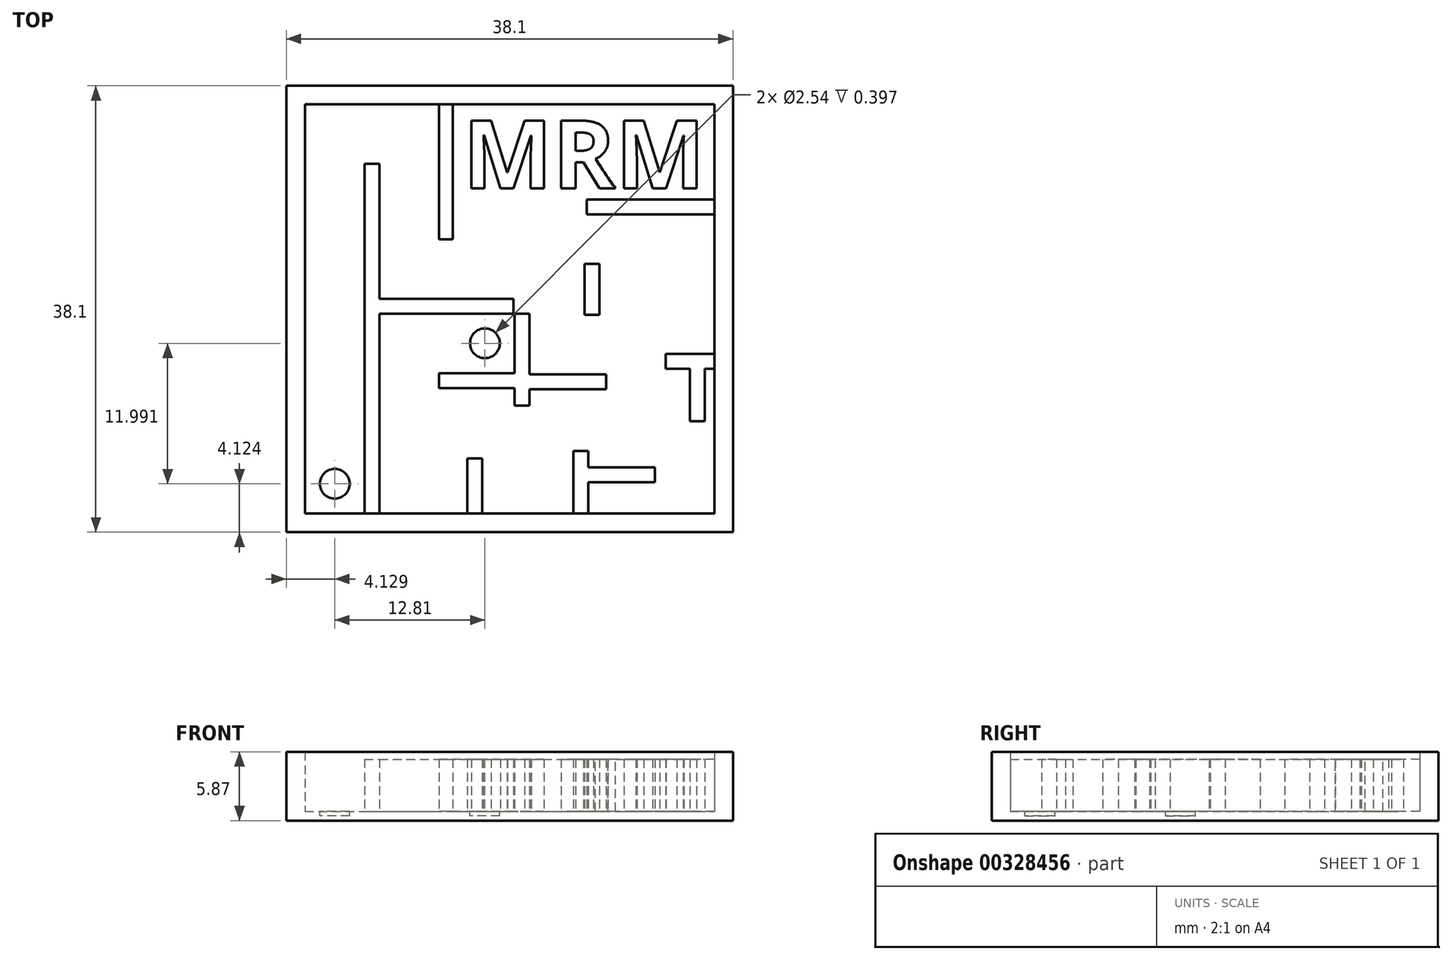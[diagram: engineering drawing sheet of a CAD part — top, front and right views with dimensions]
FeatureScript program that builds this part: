
annotation { "Feature Type Name" : "Feature", "Feature Type Description" : "" }
export const myFeature = defineFeature(function(context is Context, id is Id, definition is map)
    precondition{}
    {
        {
            var Q0;
            Q0=qCreatedBy(makeId("Top.planeOp"),FACE);
            var sketch = newSketch(context, id + "F0", { "sketchPlane" : qUnion([Q0])});
            skLineSegment(sketch, "E0.bottom", {"start": v(-20, 23.3) * mm, "end": v(18.1, 23.3) * mm});
            skLineSegment(sketch, "E0.top", {"start": v(-20, -14.8) * mm, "end": v(18.1, -14.8) * mm});
            skLineSegment(sketch, "E0.left", {"start": v(-20, 23.3) * mm, "end": v(-20, -14.8) * mm});
            skLineSegment(sketch, "E0.right", {"start": v(18.1, 23.3) * mm, "end": v(18.1, -14.8) * mm});
            skSolve(sketch);
        }
        {
            var Q0;
            Q0=makeQuery(id+"F0.imprint","IMPRINT",FACE,{"disambiguationData":[TD([[makeQuery(id+"F0.imprint","IMPRINT",EDGE,{"derivedFrom":sQuery(id+"F0.wireOp",EDGE,"E0.bottom")}),-1.0]])]});
            extrude(context, id + "F1", {"entities" : qUnion([Q0]), "oppositeDirection" : true, "depth" : 0.8 * mm});
        }
        {
            var Q0;
            Q0=makeQuery(id+"F1.opExtrude","CAP_FACE",FACE,{"disambiguationData":[OSD([sQuery(id+"F0.wireOp",EDGE,"E0.bottom"),sQuery(id+"F0.wireOp",EDGE,"E0.top"),sQuery(id+"F0.wireOp",EDGE,"E0.left"),sQuery(id+"F0.wireOp",EDGE,"E0.right")])],"isStart":true});
            var sketch = newSketch(context, id + "F2", { "sketchPlane" : qUnion([Q0])});
            skLineSegment(sketch, "E1.0", {"start": v(-18.42, 21.7) * mm, "end": v(16.5, 21.7) * mm});
            skLineSegment(sketch, "E1.1", {"start": v(-18.42, 21.7) * mm, "end": v(-18.42, -13.22) * mm});
            skLineSegment(sketch, "E1.2", {"start": v(-18.42, -13.22) * mm, "end": v(16.5, -13.22) * mm});
            skLineSegment(sketch, "E1.3", {"start": v(16.5, 21.7) * mm, "end": v(16.5, -13.22) * mm});
            skSolve(sketch);
        }
        {
            var Q0;
            Q0=makeQuery(id+"F2.imprint","IMPRINT",FACE,{"disambiguationData":[TD([[makeQuery(id+"F2.imprint","IMPRINT",EDGE,{"derivedFrom":sQuery(id+"F2.wireOp",EDGE,"E1.0")}),1.0]])]});
            extrude(context, id + "F3", {"entities" : qUnion([Q0]), "operationType" : NewBodyOperationType.ADD, "depth" : 5.08 * mm});
        }
        {
            var Q0;
            Q0=makeQuery(id+"F1.opExtrude","CAP_FACE",FACE,{"disambiguationData":[OSD([sQuery(id+"F0.wireOp",EDGE,"E0.bottom"),sQuery(id+"F0.wireOp",EDGE,"E0.top"),sQuery(id+"F0.wireOp",EDGE,"E0.left"),sQuery(id+"F0.wireOp",EDGE,"E0.right")])],"isStart":true});
            var sketch = newSketch(context, id + "F4", { "sketchPlane" : qUnion([Q0])});
            skLineSegment(sketch, "E2.bottom", {"start": v(-13.34, -13.22) * mm, "end": v(-12.07, -13.22) * mm});
            skLineSegment(sketch, "E2.top", {"start": v(-13.34, 16.63) * mm, "end": v(-12.07, 16.63) * mm});
            skLineSegment(sketch, "E2.left", {"start": v(-13.34, -13.22) * mm, "end": v(-13.34, 16.63) * mm});
            skLineSegment(sketch, "E2.right", {"start": v(-12.07, -13.22) * mm, "end": v(-12.07, 16.63) * mm});
            skLineSegment(sketch, "E3.bottom", {"start": v(-5.82, 21.7) * mm, "end": v(-7, 21.7) * mm});
            skLineSegment(sketch, "E3.top", {"start": v(-5.82, 10.2) * mm, "end": v(-7, 10.2) * mm});
            skLineSegment(sketch, "E3.left", {"start": v(-5.82, 21.7) * mm, "end": v(-5.82, 15.9) * mm});
            skLineSegment(sketch, "E3.right", {"start": v(-7, 21.7) * mm, "end": v(-7, 10.2) * mm});
            skLineSegment(sketch, "E4.bottom", {"start": v(-12.07, 5.13) * mm, "end": v(-0.64, 5.13) * mm});
            skLineSegment(sketch, "E4.top", {"start": v(-12.07, 3.86) * mm, "end": v(-0.53, 3.86) * mm});
            skLineSegment(sketch, "E4.left", {"start": v(-12.07, 5.13) * mm, "end": v(-12.07, 3.86) * mm});
            skLineSegment(sketch, "E4.right", {"start": v(-0.64, 5.13) * mm, "end": v(-0.64, 3.86) * mm});
            skLineSegment(sketch, "E5.bottom", {"start": v(16.5, -0.84) * mm, "end": v(15.7, -0.84) * mm});
            skLineSegment(sketch, "E5.top", {"start": v(16.5, 0.43) * mm, "end": v(12.34, 0.43) * mm});
            skLineSegment(sketch, "E5.left", {"start": v(16.5, -0.84) * mm, "end": v(16.5, 0.43) * mm});
            skLineSegment(sketch, "E5.right", {"start": v(12.34, -0.84) * mm, "end": v(12.34, 0.43) * mm});
            skLineSegment(sketch, "E6.bottom", {"start": v(-0.64, 3.86) * mm, "end": v(0.73, 3.86) * mm});
            skLineSegment(sketch, "E6.left", {"start": v(-0.53, 3.86) * mm, "end": v(-0.53, -1.22) * mm});
            skLineSegment(sketch, "E6.right", {"start": v(0.73, 3.86) * mm, "end": v(0.73, -1.33) * mm});
            skLineSegment(sketch, "E7.bottom", {"start": v(-0.53, -1.22) * mm, "end": v(-7, -1.22) * mm});
            skLineSegment(sketch, "E7.top", {"start": v(-0.53, -2.5) * mm, "end": v(-7, -2.5) * mm});
            skLineSegment(sketch, "E7.right", {"start": v(-7, -1.22) * mm, "end": v(-7, -2.5) * mm});
            skLineSegment(sketch, "E8.bottom", {"start": v(4.49, -13.22) * mm, "end": v(5.76, -13.22) * mm});
            skLineSegment(sketch, "E8.top", {"start": v(4.49, -7.87) * mm, "end": v(5.76, -7.87) * mm});
            skLineSegment(sketch, "E8.left", {"start": v(4.49, -13.22) * mm, "end": v(4.49, -7.87) * mm});
            skLineSegment(sketch, "E8.right", {"start": v(5.76, -13.22) * mm, "end": v(5.76, -10.54) * mm});
            skPoint(sketch, "E9.oppositeSnap0", {"position": v(5.76, -10.54) * mm});
            skLineSegment(sketch, "E9.bottom", {"start": v(5.76, -9.27) * mm, "end": v(11.42, -9.27) * mm});
            skLineSegment(sketch, "E9.top", {"start": v(5.76, -10.54) * mm, "end": v(11.42, -10.54) * mm});
            skLineSegment(sketch, "E9.right", {"start": v(11.42, -9.27) * mm, "end": v(11.42, -10.54) * mm});
            skLineSegment(sketch, "E10.top", {"start": v(14.42, -5.34) * mm, "end": v(15.7, -5.34) * mm});
            skLineSegment(sketch, "E10.left", {"start": v(14.42, -0.84) * mm, "end": v(14.42, -5.34) * mm});
            skLineSegment(sketch, "E10.right", {"start": v(15.7, -0.84) * mm, "end": v(15.7, -5.34) * mm});
            skLineSegment(sketch, "E11.bottom", {"start": v(-4.56, -13.22) * mm, "end": v(-3.29, -13.22) * mm});
            skLineSegment(sketch, "E11.top", {"start": v(-4.56, -8.5) * mm, "end": v(-3.29, -8.5) * mm});
            skLineSegment(sketch, "E11.left", {"start": v(-4.56, -13.22) * mm, "end": v(-4.56, -8.5) * mm});
            skLineSegment(sketch, "E11.right", {"start": v(-3.29, -13.22) * mm, "end": v(-3.29, -8.5) * mm});
            skLineSegment(sketch, "E12.bottom", {"start": v(0.73, -2.6) * mm, "end": v(7.26, -2.6) * mm});
            skLineSegment(sketch, "E12.top", {"start": v(0.73, -1.33) * mm, "end": v(5.81, -1.33) * mm});
            skLineSegment(sketch, "E12.right", {"start": v(7.26, -2.6) * mm, "end": v(7.26, -1.33) * mm});
            skLineSegment(sketch, "E13.trimOffspring", {"start": v(-5.82, 16.23) * mm, "end": v(-5.82, 10.2) * mm});
            skLineSegment(sketch, "E14.trimOffspring", {"start": v(-2.03, 5.13) * mm, "end": v(-0.64, 5.13) * mm});
            skLineSegment(sketch, "E15.trimOffspring", {"start": v(5.75, -1.33) * mm, "end": v(7.26, -1.33) * mm});
            skLineSegment(sketch, "E16.trimOffspring", {"start": v(14.42, -0.84) * mm, "end": v(12.34, -0.84) * mm});
            skLineSegment(sketch, "E17.trimOffspring", {"start": v(5.76, -9.27) * mm, "end": v(5.76, -7.87) * mm});
            skLineSegment(sketch, "E18.top", {"start": v(6.71, 8.1) * mm, "end": v(5.44, 8.1) * mm});
            skLineSegment(sketch, "E19.bottom", {"start": v(5.44, 8.1) * mm, "end": v(6.71, 8.1) * mm});
            skLineSegment(sketch, "E19.top", {"start": v(5.44, 3.75) * mm, "end": v(6.71, 3.75) * mm});
            skLineSegment(sketch, "E19.left", {"start": v(5.44, 8.1) * mm, "end": v(5.44, 3.75) * mm});
            skLineSegment(sketch, "E19.right", {"start": v(6.71, 8.1) * mm, "end": v(6.71, 3.75) * mm});
            skLineSegment(sketch, "E20.bottom", {"start": v(16.5, 12.32) * mm, "end": v(5.6, 12.32) * mm});
            skLineSegment(sketch, "E20.top", {"start": v(16.5, 13.59) * mm, "end": v(5.6, 13.59) * mm});
            skLineSegment(sketch, "E20.left", {"start": v(16.5, 12.32) * mm, "end": v(16.5, 13.59) * mm});
            skLineSegment(sketch, "E20.right", {"start": v(5.6, 12.32) * mm, "end": v(5.6, 13.59) * mm});
            skLineSegment(sketch, "E21.bottom", {"start": v(8.22, 13.59) * mm, "end": v(9.49, 13.59) * mm});
            skText(sketch, "E22", { "text": "MRM", "fontName": "OpenSans-Bold.ttf"});
            skLineSegment(sketch, "E23", {"start": v(0.73, -2.6) * mm, "end": v(0.73, -4) * mm});
            skLineSegment(sketch, "E24", {"start": v(0.73, -4) * mm, "end": v(-0.53, -4) * mm});
            skLineSegment(sketch, "E25", {"start": v(-0.53, -4) * mm, "end": v(-0.53, -2.5) * mm});
            const initialGuessF4  = {"E22": [-0.00494, 0.01453, 1, 0, 0.00584]};
            skSetInitialGuess(sketch, initialGuessF4);
            skSolve(sketch);
        }
        {
            var Q0;
            Q0=makeQuery(id+"F4.imprint","IMPRINT",FACE,{"disambiguationData":[TD([[makeQuery(id+"F4.imprint","IMPRINT",EDGE,{"derivedFrom":sQuery(id+"F4.wireOp",EDGE,"E3.bottom")}),-1.0]])]});
            var Q1;
            Q1=makeQuery(id+"F4.imprint","IMPRINT",FACE,{"disambiguationData":[TD([[makeQuery(id+"F4.imprint","IMPRINT",EDGE,{"derivedFrom":sQuery(id+"F4.wireOp",EDGE,"E5.bottom")}),-1.0]])]});
            var Q2;
            Q2=makeQuery(id+"F4.imprint","IMPRINT",FACE,{"disambiguationData":[TD([[makeQuery(id+"F4.imprint","IMPRINT",EDGE,{"derivedFrom":sQuery(id+"F4.wireOp",EDGE,"E6.top")}),1.0]])]});
            var Q3;
            Q3=makeQuery(id+"F4.imprint","IMPRINT",FACE,{"disambiguationData":[TD([[makeQuery(id+"F4.imprint","IMPRINT",EDGE,{"derivedFrom":sQuery(id+"F4.wireOp",EDGE,"E8.bottom")}),1.0]])]});
            var Q4;
            {var subQ0=sQuery(id+"F4.wireOp",EDGE,"E11.bottom");Q4=makeQuery(id+"F4.imprint","IMPRINT",FACE,{"disambiguationData":[TD([[makeQuery(id+"F4.imprint","IMPRINT",EDGE,{"derivedFrom":subQ0}),1.0]])]});}
            var Q5;
            Q5=makeQuery(id+"F4.imprint","IMPRINT",FACE,{"disambiguationData":[TD([[makeQuery(id+"F4.imprint","IMPRINT",EDGE,{"derivedFrom":sQuery(id+"F4.wireOp",EDGE,"E19.bottom")}),-1.0]])]});
            var Q6;
            Q6=makeQuery(id+"F4.imprint","IMPRINT",FACE,{"disambiguationData":[TD([[makeQuery(id+"F4.imprint","IMPRINT",EDGE,{"derivedFrom":sQuery(id+"F4.wireOp",EDGE,"Trm1tnAc-shaY-joJB-pkr8-oYNgstYqohEI.bottom")}),-1.0]])]});
            var Q7;
            Q7=makeQuery(id+"F4.imprint","IMPRINT",FACE,{"disambiguationData":[TD([[makeQuery(id+"F4.imprint","IMPRINT",EDGE,{"derivedFrom":sQuery(id+"F4.wireOp",EDGE,"E20.bottom")}),-1.0]])]});
            var Q8;
            Q8=makeQuery(id+"F4.imprint","IMPRINT",FACE,{"disambiguationData":[TD([[makeQuery(id+"F4.imprint","IMPRINT",EDGE,{"derivedFrom":sQuery(id+"F4.wireOp",EDGE,"E4.bottom")}),-1.0]])]});
            var Q9;
            {var subQ1=sQuery(id+"F4.wireOp",EDGE,"E2.bottom");Q9=makeQuery(id+"F4.imprint","IMPRINT",FACE,{"disambiguationData":[TD([[makeQuery(id+"F4.imprint","IMPRINT",EDGE,{"derivedFrom":subQ1}),1.0]])]});}
            extrude(context, id + "F5", {"entities" : qUnion([Q0, Q1, Q2, Q3, Q4, Q5, Q6, Q7, Q8, Q9]), "operationType" : NewBodyOperationType.ADD, "depth" : 4.44 * mm});
        }
        {
            var Q0;
            Q0 = qSketchRegion(id + "F4", true);
            extrude(context, id + "F6", {"entities" : qUnion([Q0]), "operationType" : NewBodyOperationType.ADD, "depth" : 4.44 * mm});
        }
        {
            var Q0;
            {var subQ13=sQuery(id+"F4.wireOp",EDGE,"E2.top");Q0=makeQuery(id+"F4.imprint","IMPRINT",FACE,{"disambiguationData":[TD([[makeQuery(id+"F4.imprint","IMPRINT",EDGE,{"derivedFrom":subQ13}),1.0]])]});}
            var sketch = newSketch(context, id + "F7", { "sketchPlane" : qUnion([Q0])});
            skCircle(sketch, "E26", {"center": v(-15.88, -10.68) * mm, "radius": 1.27 * mm});
            skCircle(sketch, "E27", {"center": v(-3.07, 1.32) * mm, "radius": 1.27 * mm});
            skSolve(sketch);
        }
        {
            var Q0;
            Q0=makeQuery(id+"F7.imprint","IMPRINT",FACE,{"disambiguationData":[TD([[makeQuery(id+"F7.imprint","IMPRINT",EDGE,{"derivedFrom":sQuery(id+"F7.wireOp",EDGE,"E27")}),1.0]])]});
            var Q1;
            Q1=makeQuery(id+"F7.imprint","IMPRINT",FACE,{"disambiguationData":[TD([[makeQuery(id+"F7.imprint","IMPRINT",EDGE,{"derivedFrom":sQuery(id+"F7.wireOp",EDGE,"E26")}),1.0]])]});
            extrude(context, id + "F8", {"entities" : qUnion([Q0, Q1]), "operationType" : NewBodyOperationType.REMOVE, "oppositeDirection" : true, "depth" : 0.4 * mm});
        }
    });
